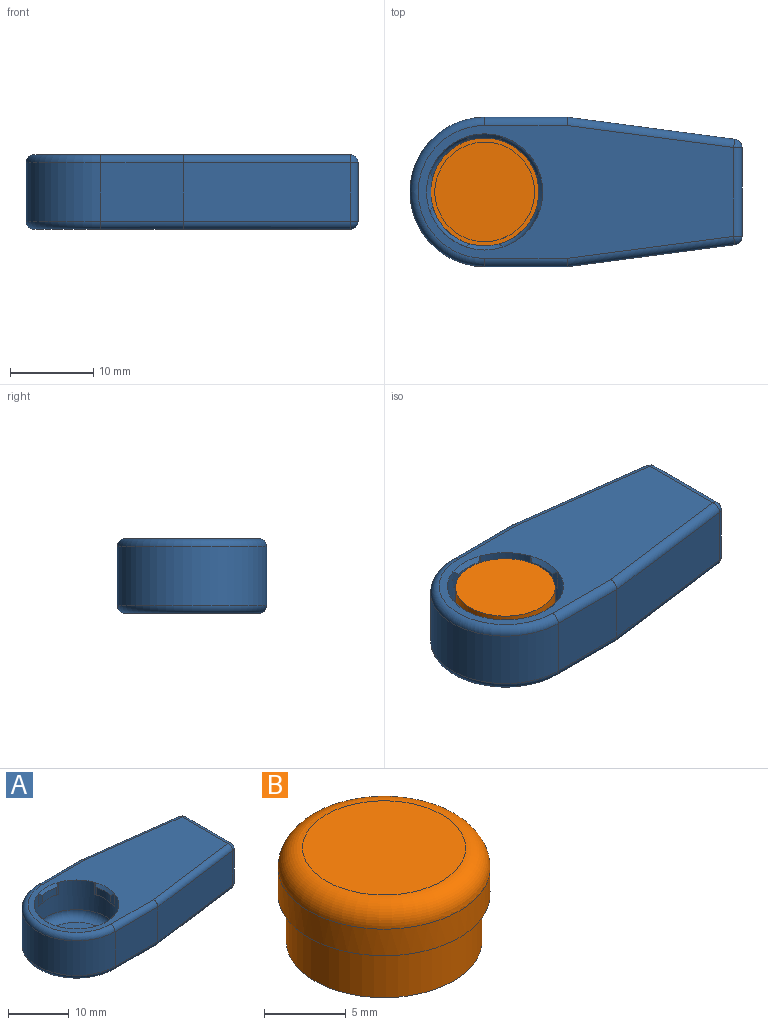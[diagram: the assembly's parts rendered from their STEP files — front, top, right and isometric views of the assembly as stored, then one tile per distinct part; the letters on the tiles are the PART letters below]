
ASSEMBLY  parts=2 mates=1
PART A: 70 faces, bbox 40.9x19.7x9.5 mm
  f0: plane 3.53x0.28mm, normal (0,0,-1), area 0.2mm2, adj f1,f67,f68,f69
  f1: plane 2.47x0.65mm, normal (-0.88,0.47,0), area 1.4mm2, adj f0,f2,f66,f67,f69
  f2: cylinder r=7mm len=14mm, axis (0,0,1), area 217.4mm2, adj f1,f3,f7,f8,f9,f13,f14,f15
  f3: plane 2.47x0.65mm, normal (0.47,-0.88,0), area 1.4mm2, adj f2,f4,f5,f6,f7
  f4: plane 3.53x0.28mm, normal (0,0,-1), area 0.2mm2, adj f3,f5,f7,f8
  f5: cylinder r=6.5mm len=3.4mm, axis (0,0,1), area 5.2mm2, adj f3,f4,f6,f8
  f6: cone r=6.5mm half-angle=45deg, axis (0,0,1), area 2.9mm2, adj f3,f5,f8,f21
  f7: cone r=7mm half-angle=45deg, axis (0,0,-1), area 2.6mm2, adj f2,f3,f4,f8
  f8: plane 2.47x0.65mm, normal (-0.47,-0.88,0), area 1.4mm2, adj f2,f4,f5,f6,f7
  f9: plane 2.47x0.65mm, normal (0.88,0.47,0), area 1.4mm2, adj f2,f10,f11,f12,f13
  f10: plane 3.53x0.28mm, normal (0,0,-1), area 0.2mm2, adj f9,f11,f13,f14
  f11: cylinder r=6.5mm len=3.4mm, axis (0,0,1), area 5.2mm2, adj f9,f10,f12,f14
  f12: cone r=6.5mm half-angle=45deg, axis (0,0,1), area 2.9mm2, adj f9,f11,f14,f21
  f13: cone r=7mm half-angle=45deg, axis (0,0,-1), area 2.6mm2, adj f2,f9,f10,f14
  f14: plane 2.47x0.65mm, normal (0.88,-0.47,0), area 1.4mm2, adj f2,f10,f11,f12,f13
  f15: plane 2.47x0.65mm, normal (-0.47,0.88,0), area 1.4mm2, adj f2,f16,f17,f18,f19
  f16: plane 3.53x0.28mm, normal (0,0,-1), area 0.2mm2, adj f15,f17,f19,f20
  f17: cylinder r=6.5mm len=3.4mm, axis (0,0,1), area 5.2mm2, adj f15,f16,f18,f20
  f18: cone r=6.5mm half-angle=45deg, axis (0,0,1), area 2.9mm2, adj f15,f17,f20,f21
  f19: cone r=7mm half-angle=45deg, axis (0,0,-1), area 2.6mm2, adj f2,f15,f16,f20
  f20: plane 2.47x0.65mm, normal (0.47,0.88,0), area 1.4mm2, adj f2,f16,f17,f18,f19
  f21: plane 38x16mm, normal (0,0,1), area 373.6mm2, adj f2,f6,f12,f18,f22,f59,f60,f61
  f22: cylinder r=1mm len=10mm, axis (-1,0,0), area 15.7mm2, adj f21,f23,f59,f63
  f23: plane 10x7mm, normal (0,-1,0), area 70mm2, adj f22,f24,f57,f58
  f24: cylinder r=1mm len=10mm, axis (1,0,0), area 15.7mm2, adj f23,f25,f55,f56
  f25: plane 38.19x16.19mm, normal (0,0,-1), area 517.1mm2, adj f24,f26,f49,f50,f51,f52,f53,f54
  f26: bspline ~4.69x4.06mm, area 25.4mm2, adj f25,f27,f49,f51
  f27: cylinder r=2.15mm len=11.5mm, axis (1,0,0), area 143.7mm2, adj f26,f28,f29,f30,f31,f32,f33,f34
  f28: bspline ~4.06x2.34mm, area 0mm2, adj f27,f29
  f29: bspline ~4.12x2.38mm, area 0.3mm2, adj f27,f28,f30
  f30: bspline ~4.06x2.34mm, area 1.3mm2, adj f27,f29,f49
  f31: plane 4.3x4.3mm, normal (1,0,0), area 14.5mm2, adj f27
  f32: plane 1.86x0.27mm, normal (0,0,-1), area 0.3mm2, adj f27,f33,f34
  f33: bspline ~2.03x0.91mm, area 0mm2, adj f27,f32,f34
  f34: bspline ~3.09x2.38mm, area 0.1mm2, adj f27,f32,f33,f35
  f35: bspline ~3.04x2.34mm, area 0.7mm2, adj f27,f34,f36
  f36: cylinder r=1.65mm len=1.84mm, axis (0,0,1), area 0.3mm2, adj f27,f35,f37
  f37: bspline ~4.06x2.34mm, area 1.3mm2, adj f27,f36,f38
  f38: bspline ~4.12x2.38mm, area 0.5mm2, adj f27,f37,f50
  f39: cone r=2.15mm half-angle=45deg, axis (1,0,0), area 10.7mm2, adj f27,f40,f62
  f40: plane 10.72x7mm, normal (1,0,0), area 53.1mm2, adj f39,f41,f44,f53,f62
  f41: cylinder r=1mm len=7mm, axis (0,0,1), area 10.1mm2, adj f40,f42,f43,f58
  f42: sphere r=1mm, area 1.4mm2, adj f41,f62,f63
  f43: sphere r=1mm, area 1.4mm2, adj f41,f53,f56
  f44: cylinder r=1mm len=7mm, axis (0,0,1), area 10.1mm2, adj f40,f45,f46,f48
  f45: sphere r=1mm, area 0.9mm2, adj f44,f61,f62
  f46: plane 20.13x7mm, normal (0.13,0.99,0), area 142.1mm2, adj f44,f47,f54,f61
  f47: plane 10x7mm, normal (0,1,0), area 70mm2, adj f46,f52,f57,f60
  f48: sphere r=1mm, area 0.9mm2, adj f44,f53,f54
  f49: cylinder r=1.65mm len=3.75mm, axis (0,0,1), area 9.6mm2, adj f25,f26,f27,f30,f50
  f50: bspline ~4.69x4.06mm, area 25.7mm2, adj f25,f27,f38,f49,f51
  f51: bspline ~4.76x4.12mm, area 6.3mm2, adj f25,f26,f27,f50
  f52: cylinder r=1mm len=10mm, axis (-1,0,0), area 15.7mm2, adj f25,f47,f54,f55
  f53: cylinder r=1mm len=10.72mm, axis (0,1,0), area 16.8mm2, adj f25,f40,f43,f48
  f54: cylinder r=1mm len=20.26mm, axis (0.99,-0.13,0), area 31.8mm2, adj f25,f46,f48,f52
  f55: torus R=8mm, axis (0,0,1), area 42.6mm2, adj f24,f25,f52,f57
  f56: cylinder r=1mm len=20.26mm, axis (0.99,0.13,0), area 31.8mm2, adj f24,f25,f43,f58
  f57: cylinder r=9mm len=18mm, axis (0,0,-1), area 197.9mm2, adj f23,f47,f55,f59
  f58: plane 20.13x7mm, normal (0.13,-0.99,0), area 142.1mm2, adj f23,f41,f56,f63
  f59: torus R=8mm, axis (0,0,1), area 42.6mm2, adj f21,f22,f57,f60
  f60: cylinder r=1mm len=10mm, axis (1,0,0), area 15.7mm2, adj f21,f47,f59,f61
  f61: cylinder r=1mm len=20.26mm, axis (0.99,-0.13,0), area 31.8mm2, adj f21,f45,f46,f60
  f62: cylinder r=1mm len=10.72mm, axis (0,-1,0), area 16.7mm2, adj f21,f39,f40,f42,f45
  f63: cylinder r=1mm len=20.26mm, axis (0.99,0.13,0), area 31.8mm2, adj f21,f22,f42,f58
  f64: torus R=5.5mm, axis (0,0,1), area 95.6mm2, adj f2,f65
  f65: plane 11x11mm, normal (0,0,1), area 95mm2, adj f64
  f66: cone r=6.5mm half-angle=45deg, axis (0,0,1), area 2.9mm2, adj f1,f21,f67,f68
  f67: cylinder r=6.5mm len=3.4mm, axis (0,0,1), area 5.2mm2, adj f0,f1,f66,f68
  f68: plane 2.47x0.65mm, normal (-0.88,-0.47,0), area 1.4mm2, adj f0,f2,f66,f67,f69
  f69: cone r=7mm half-angle=45deg, axis (0,0,-1), area 2.6mm2, adj f0,f1,f2,f68
PART B: 6 faces, bbox 14.1x14.1x7 mm
  f0: plane 12x12mm, normal (0,0,-1), area 113.1mm2, adj f4
  f1: plane 10x10mm, normal (0,0,1), area 78.5mm2, adj f5
  f2: cylinder r=6.5mm len=13mm, axis (0,0,1), area 81.7mm2, adj f3,f5
  f3: plane 13x13mm, normal (0,0,-1), area 19.6mm2, adj f2,f4
  f4: cylinder r=6mm len=12mm, axis (0,0,1), area 131.9mm2, adj f0,f3
  f5: torus R=5mm, axis (0,0,-1), area 88.2mm2, adj f1,f2
PLACE A t=(12.84,27.58,26.04)mm
PLACE B rot(axis=(-1,0,0),180deg) t=(1.84,27.58,34.87)mm
MATE slider B.f5 <-> A.f2  axis (0,0,-1) through (1.84,27.58,30.37)mm
